# Revit family: Sanitary_Storage_hansgrohe_56093XXX-XtraStoris-Original-Wall-niche___
name_source: partatom
category: Furniture
revit_build: Autodesk Revit 2018 (Build: 20170223_1515(x64)
units: mm (PartAtom-declared; Revit-internal decimal feet)

## family parameters
Cut with Voids When Loaded = Yes
Host = Face
OmniClass Number = 23.31.25.13
OmniClass Title = Bathroom Cabinets
Room Calculation Point = No
Shared = No

## types (3) — shared parameters
BIMobject category = Storage
Description = XtraStoris Original Wall niche with frame 300/300/70
Design country = Germany
Edition number = 1
IFC Classification = Furnishing Element
Manufacturer = Hansgrohe
Manufacturer country = Germany
Manufacturer name = hansgrohe
Masterformat 2014 Code = 12 35 30.23
Masterformat 2014 Description = Bathroom Casework
Model = 56093XXX
OmniClass Code = 23-31 25 13
OmniClass Description = Bathroom Cabinets
Product Guid = c13ec986-8b8a-4e49-9a67-046bb1e6d826
Product SKU = 56093XXX
Product data url = https://bimobject.com
Product family = uBox universal
Product group = Concealed basic set shower drains
Product name = 56093XXX XtraStoris Original Wall niche with frame 300/300/70
Product url = https://www.hansgrohe.com
QR code = https://bimobject.com
UNSPSC Code = 301815
URL = https://www.hansgrohe.com
Uniclass 2015 Code = Pr_40_30_78_03
Uniclass 2015 Name = Bathroom cabinets
Uniformat II Code = E2010
Uniformat II Description = Fixed Furnishings
Weight Net (Kg) = 1.9
zero-valued in all types: Default Elevation

## per-type parameters (varying)
| type | Material 1 |
| 380 Concretegrey | Hansgrohe - Metal - 380 Concretegrey |
| 700 Matte White | Hansgrohe - Metal - 700 Matte White |
| 670 Matte Black | Hansgrohe - Metal - 670 Matte Black |

## geometry (parser evidence)
native form markers: Sweep x4
no freeform markers — native parametric forms only
